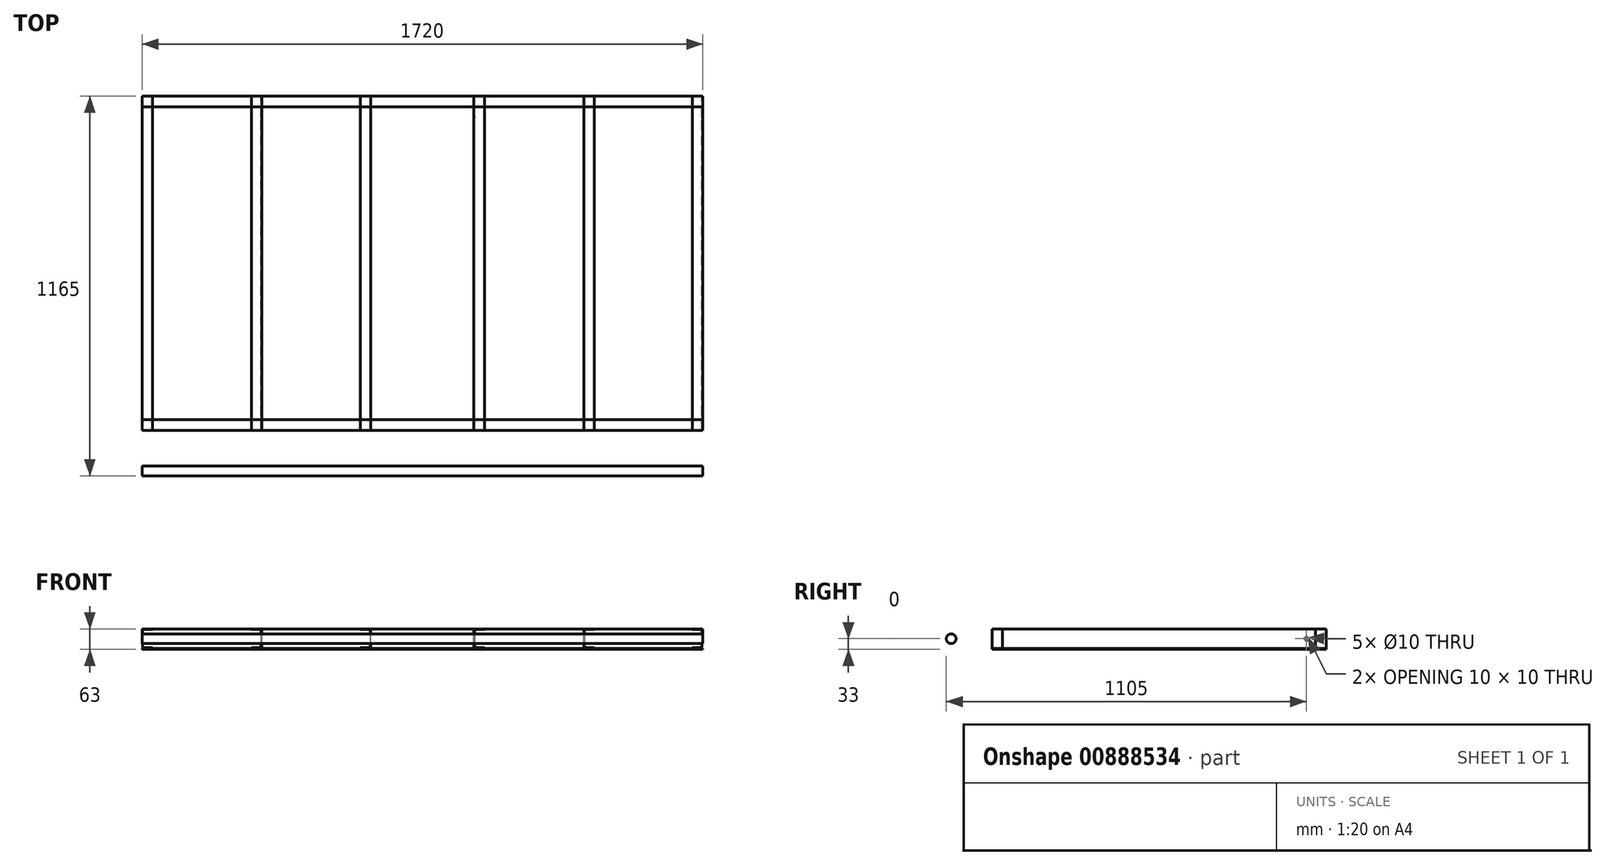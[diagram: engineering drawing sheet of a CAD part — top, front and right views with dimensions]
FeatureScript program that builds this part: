
annotation { "Feature Type Name" : "Feature", "Feature Type Description" : "" }
export const myFeature = defineFeature(function(context is Context, id is Id, definition is map)
    precondition{}
    {
        {
            var Q0;
            Q0=qCreatedBy(makeId("Front.planeOp"),FACE);
            var sketch = newSketch(context, id + "F0", { "sketchPlane" : qUnion([Q0])});
            skLineSegment(sketch, "E0", {"start": v(0, 0) * mm, "end": v(0, 60) * mm});
            skLineSegment(sketch, "E1", {"start": v(0, 60) * mm, "end": v(32, 60) * mm});
            skLineSegment(sketch, "E2.0", {"start": v(2, 58) * mm, "end": v(32, 58) * mm});
            skLineSegment(sketch, "E3", {"start": v(32, 60) * mm, "end": v(32, 58) * mm});
            skLineSegment(sketch, "E4", {"start": v(0, 30) * mm, "end": v(30.45, 30) * mm, "construction": true});
            skLineSegment(sketch, "E5.MirrorCS", {"start": v(32, 0) * mm, "end": v(32, 2) * mm});
            skLineSegment(sketch, "E6.MirrorCS", {"start": v(2, 2) * mm, "end": v(32, 2) * mm});
            skLineSegment(sketch, "E7.MirrorCS", {"start": v(0, 0) * mm, "end": v(32, 0) * mm});
            skLineSegment(sketch, "E8", {"start": v(2, 58) * mm, "end": v(2, 2) * mm});
            skSolve(sketch);
        }
        {
            var Q0;
            Q0=makeQuery(id+"F0.imprint","IMPRINT",FACE,{"disambiguationData":[TD([[makeQuery(id+"F0.imprint","IMPRINT",EDGE,{"derivedFrom":sQuery(id+"F0.wireOp",EDGE,"E0")}),-1.0]])]});
            extrude(context, id + "F1", {"entities" : qUnion([Q0]), "endBound" : BoundingType.SYMMETRIC, "depth" : 1025 * mm, "offsetDistance" : 25 * mm});
        }
        {
            var Q0;
            Q0=makeQuery(id+"F1.opExtrude","SWEPT_BODY",BODY,{"disambiguationData":[OSD([sQuery(id+"F0.wireOp",EDGE,"E0"),sQuery(id+"F0.wireOp",EDGE,"E1"),sQuery(id+"F0.wireOp",EDGE,"E2.0"),sQuery(id+"F0.wireOp",EDGE,"E3"),sQuery(id+"F0.wireOp",EDGE,"E5.MirrorCS"),sQuery(id+"F0.wireOp",EDGE,"E6.MirrorCS"),sQuery(id+"F0.wireOp",EDGE,"E7.MirrorCS"),sQuery(id+"F0.wireOp",EDGE,"E8")])]});
            var Q1;
            Q1=makeQuery(id+"F1.opExtrude","CAP_EDGE",EDGE,{"disambiguationData":[OSD([sQuery(id+"F0.wireOp",EDGE,"E1")])],"isStart":false});
            transform(context, id + "F2", {"entities" : qUnion([Q0]), "transformType" : TransformType.TRANSLATION_DISTANCE, "transformDirection" : qUnion([Q1]), "distance" : 158.25 * mm, "makeCopy" : false});
        }
        {
            var Q0;
            Q0=qCreatedBy(makeId("Top.planeOp"),FACE);
            var sketch = newSketch(context, id + "F3", { "sketchPlane" : qUnion([Q0])});
            skLineSegment(sketch, "E9.bottom", {"start": v(-860, 512.5) * mm, "end": v(860, 512.5) * mm});
            skLineSegment(sketch, "E9.top", {"start": v(-860, -512.5) * mm, "end": v(860, -512.5) * mm});
            skLineSegment(sketch, "E9.left", {"start": v(-860, 512.5) * mm, "end": v(-860, -512.5) * mm});
            skLineSegment(sketch, "E9.right", {"start": v(860, 512.5) * mm, "end": v(860, -512.5) * mm});
            skLineSegment(sketch, "E10", {"start": v(0, -494.46) * mm, "end": v(0, 621.74) * mm, "construction": true});
            skLineSegment(sketch, "E11", {"start": v(-634.69, 0) * mm, "end": v(657.83, 0) * mm, "construction": true});
            skSolve(sketch);
        }
        {
            var Q0;
            Q0 = qSketchRegion(id + "F3", true);
            extrude(context, id + "F4", {"entities" : qUnion([Q0]), "oppositeDirection" : true, "depth" : 3 * mm, "offsetDistance" : 25 * mm});
        }
        {
            var Q0;
            Q0=makeQuery(id+"F1.opExtrude","SWEPT_BODY",BODY,{"disambiguationData":[OSD([sQuery(id+"F0.wireOp",EDGE,"E0"),sQuery(id+"F0.wireOp",EDGE,"E1"),sQuery(id+"F0.wireOp",EDGE,"E2.0"),sQuery(id+"F0.wireOp",EDGE,"E3"),sQuery(id+"F0.wireOp",EDGE,"E5.MirrorCS"),sQuery(id+"F0.wireOp",EDGE,"E6.MirrorCS"),sQuery(id+"F0.wireOp",EDGE,"E7.MirrorCS"),sQuery(id+"F0.wireOp",EDGE,"E8")])]});
            var Q1;
            Q1=makeQuery(id+"F4.opExtrude","CAP_EDGE",EDGE,{"disambiguationData":[OSD([sQuery(id+"F3.wireOp",EDGE,"E9.top")])],"isStart":true});
            transform(context, id + "F5", {"entities" : qUnion([Q0]), "transformType" : TransformType.TRANSLATION_DISTANCE, "transformDirection" : qUnion([Q1]), "distance" : 337 * mm, "makeCopy" : true});
        }
        {
            var Q0;
            Q0=makeQuery(id+"F4.opExtrude","CAP_FACE",FACE,{"disambiguationData":[OSD([sQuery(id+"F3.wireOp",EDGE,"E9.bottom"),sQuery(id+"F3.wireOp",EDGE,"E9.top"),sQuery(id+"F3.wireOp",EDGE,"E9.left"),sQuery(id+"F3.wireOp",EDGE,"E9.right")])],"isStart":true});
            cPlane(context, id + "F6", {"entities" : qUnion([Q0]), "cplaneType" : CPlaneType.OFFSET, "offset" : 0 * mm, "width" : 150 * mm, "height" : 150 * mm});
        }
        {
            var Q0;
            Q0=qCreatedBy(id+"F6.planeOp",FACE);
            var sketch = newSketch(context, id + "F7", { "sketchPlane" : qUnion([Q0])});
            skLineSegment(sketch, "E12.0", {"start": v(527.25, -512.5) * mm, "end": v(527.25, 512.5) * mm, "construction": true});
            skLineSegment(sketch, "E13.0", {"start": v(860, 512.5) * mm, "end": v(860, -512.5) * mm, "construction": true});
            skLineSegment(sketch, "E14", {"start": v(527.25, 0) * mm, "end": v(828, 0) * mm, "construction": true});
            skPoint(sketch, "E15.startSnap0", {"position": v(693.62, 0) * mm});
            skLineSegment(sketch, "E16", {"start": v(828, 189.17) * mm, "end": v(828, -311.1) * mm, "construction": true});
            skPoint(sketch, "E17.orphan", {"position": v(860, 0) * mm});
            skLineSegment(sketch, "E18", {"start": v(677.62, 0) * mm, "end": v(677.62, 369.47) * mm, "construction": true});
            skSolve(sketch);
        }
        {
            var Q0;
            Q0=sQuery(id+"F7.wireOp",EDGE,"E14");
            cPoint(context, id + "F8", {"entities" : qUnion([Q0]), "parameter" : 0.5});
        }
        {
            var Q0;
            Q0 = qCreatedBy(id + "F8" ,VERTEX);
            var Q1;
            Q1=sQuery(id+"F7.wireOp",EDGE,"E14");
            cPlane(context, id + "F9", {"entities" : qUnion([Q0, Q1]), "cplaneType" : CPlaneType.LINE_POINT, "offset" : 25 * mm, "width" : 150 * mm, "height" : 150 * mm});
        }
        {
            var Q0;
            Q0=makeQuery(id+"F5.opPattern","COPY",BODY,{"derivedFrom":makeQuery(id+"F1.opExtrude","SWEPT_BODY",BODY,{"disambiguationData":[OSD([sQuery(id+"F0.wireOp",EDGE,"E0"),sQuery(id+"F0.wireOp",EDGE,"E1"),sQuery(id+"F0.wireOp",EDGE,"E2.0"),sQuery(id+"F0.wireOp",EDGE,"E3"),sQuery(id+"F0.wireOp",EDGE,"E5.MirrorCS"),sQuery(id+"F0.wireOp",EDGE,"E6.MirrorCS"),sQuery(id+"F0.wireOp",EDGE,"E7.MirrorCS"),sQuery(id+"F0.wireOp",EDGE,"E8")])]}),"instanceName":"1"});
            var Q1;
            Q1=qCreatedBy(id+"F9.planeOp",FACE);
            mirror(context, id + "F10", {"entities" : qUnion([Q0]), "mirrorPlane" : qUnion([Q1])});
        }
        {
            var Q0;
            Q0=makeQuery(id+"F1.opExtrude","SWEPT_BODY",BODY,{"disambiguationData":[OSD([sQuery(id+"F0.wireOp",EDGE,"E0"),sQuery(id+"F0.wireOp",EDGE,"E1"),sQuery(id+"F0.wireOp",EDGE,"E2.0"),sQuery(id+"F0.wireOp",EDGE,"E3"),sQuery(id+"F0.wireOp",EDGE,"E5.MirrorCS"),sQuery(id+"F0.wireOp",EDGE,"E6.MirrorCS"),sQuery(id+"F0.wireOp",EDGE,"E7.MirrorCS"),sQuery(id+"F0.wireOp",EDGE,"E8")])]});
            var Q1;
            Q1=makeQuery(id+"F10.opPattern","COPY",BODY,{"derivedFrom":makeQuery(id+"F5.opPattern","COPY",BODY,{"derivedFrom":makeQuery(id+"F1.opExtrude","SWEPT_BODY",BODY,{"disambiguationData":[OSD([sQuery(id+"F0.wireOp",EDGE,"E0"),sQuery(id+"F0.wireOp",EDGE,"E1"),sQuery(id+"F0.wireOp",EDGE,"E2.0"),sQuery(id+"F0.wireOp",EDGE,"E3"),sQuery(id+"F0.wireOp",EDGE,"E5.MirrorCS"),sQuery(id+"F0.wireOp",EDGE,"E6.MirrorCS"),sQuery(id+"F0.wireOp",EDGE,"E7.MirrorCS"),sQuery(id+"F0.wireOp",EDGE,"E8")])]}),"instanceName":"1"}),"instanceName":"1"});
            var Q2;
            Q2=qCreatedBy(makeId("Right.planeOp"),FACE);
            mirror(context, id + "F11", {"entities" : qUnion([Q0, Q1]), "mirrorPlane" : qUnion([Q2])});
        }
        {
            var Q0;
            Q0=makeQuery(id+"F5.opPattern","COPY",FACE,{"derivedFrom":makeQuery(id+"F1.opExtrude","SWEPT_FACE",FACE,{"disambiguationData":[OSD([sQuery(id+"F0.wireOp",EDGE,"E0")])]}),"instanceName":"1"});
            var sketch = newSketch(context, id + "F12", { "sketchPlane" : qUnion([Q0])});
            skCircle(sketch, "E19", {"center": v(-452.5, 30) * mm, "radius": 5 * mm});
            skSolve(sketch);
        }
        {
            var Q0;
            Q0 = qSketchRegion(id + "F12", true);
            extrude(context, id + "F13", {"entities" : qUnion([Q0]), "operationType" : NewBodyOperationType.REMOVE, "endBound" : BoundingType.SYMMETRIC, "oppositeDirection" : true, "depth" : 2000 * mm, "offsetDistance" : 25 * mm});
        }
        {
            var Q0;
            Q0=makeQuery(id+"F11.opPattern","COPY",BODY,{"derivedFrom":makeQuery(id+"F1.opExtrude","SWEPT_BODY",BODY,{"disambiguationData":[OSD([sQuery(id+"F0.wireOp",EDGE,"E0"),sQuery(id+"F0.wireOp",EDGE,"E1"),sQuery(id+"F0.wireOp",EDGE,"E2.0"),sQuery(id+"F0.wireOp",EDGE,"E3"),sQuery(id+"F0.wireOp",EDGE,"E5.MirrorCS"),sQuery(id+"F0.wireOp",EDGE,"E6.MirrorCS"),sQuery(id+"F0.wireOp",EDGE,"E7.MirrorCS"),sQuery(id+"F0.wireOp",EDGE,"E8")])]}),"instanceName":"1"});
            transform(context, id + "F14", {"entities" : qUnion([Q0]), "transformType" : TransformType.TRANSLATION_3D, "dx" : -334.5 * mm, "dy" : 0 * mm, "dz" : 0 * mm, "makeCopy" : true});
        }
        {
            var Q0;
            Q0=makeQuery(id+"F10.opPattern","COPY",FACE,{"derivedFrom":makeQuery(id+"F5.opPattern","COPY",FACE,{"derivedFrom":makeQuery(id+"F1.opExtrude","SWEPT_FACE",FACE,{"disambiguationData":[OSD([sQuery(id+"F0.wireOp",EDGE,"E0")])]}),"instanceName":"1"}),"instanceName":"1"});
            var sketch = newSketch(context, id + "F15", { "sketchPlane" : qUnion([Q0])});
            skCircle(sketch, "E20", {"center": v(-637.5, 30) * mm, "radius": 15 * mm});
            skSolve(sketch);
        }
        {
            var Q0;
            Q0 = qSketchRegion(id + "F15", true);
            var Q1;
            Q1=makeQuery(id+"F11.opPattern","COPY",FACE,{"derivedFrom":makeQuery(id+"F10.opPattern","COPY",FACE,{"derivedFrom":makeQuery(id+"F5.opPattern","COPY",FACE,{"derivedFrom":makeQuery(id+"F1.opExtrude","SWEPT_FACE",FACE,{"disambiguationData":[OSD([sQuery(id+"F0.wireOp",EDGE,"E0")])]}),"instanceName":"1"}),"instanceName":"1"}),"instanceName":"1"});
            extrude(context, id + "F16", {"entities" : qUnion([Q0]), "endBound" : BoundingType.UP_TO_SURFACE, "oppositeDirection" : true, "depth" : 25 * mm, "endBoundEntityFace" : qUnion([Q1]), "offsetDistance" : 25 * mm});
        }
        {
            var Q0;
            Q0=makeQuery(id+"F10.opPattern","COPY",FACE,{"derivedFrom":makeQuery(id+"F5.opPattern","COPY",FACE,{"derivedFrom":makeQuery(id+"F1.opExtrude","SWEPT_FACE",FACE,{"disambiguationData":[OSD([sQuery(id+"F0.wireOp",EDGE,"E0")])]}),"instanceName":"1"}),"instanceName":"1"});
            var sketch = newSketch(context, id + "F17", { "sketchPlane" : qUnion([Q0])});
            skLineSegment(sketch, "E21.bottom", {"start": v(512.5, 60) * mm, "end": v(480.5, 60) * mm});
            skLineSegment(sketch, "E21.top", {"start": v(512.5, 0) * mm, "end": v(480.5, 0) * mm});
            skLineSegment(sketch, "E21.left", {"start": v(512.5, 60) * mm, "end": v(512.5, 0) * mm});
            skLineSegment(sketch, "E21.right", {"start": v(480.5, 60) * mm, "end": v(480.5, 0) * mm});
            skSolve(sketch);
        }
        {
            var Q0;
            Q0 = qSketchRegion(id + "F17", true);
            var Q1;
            Q1=makeQuery(id+"F11.opPattern","COPY",FACE,{"derivedFrom":makeQuery(id+"F10.opPattern","COPY",FACE,{"derivedFrom":makeQuery(id+"F5.opPattern","COPY",FACE,{"derivedFrom":makeQuery(id+"F1.opExtrude","SWEPT_FACE",FACE,{"disambiguationData":[OSD([sQuery(id+"F0.wireOp",EDGE,"E0")])]}),"instanceName":"1"}),"instanceName":"1"}),"instanceName":"1"});
            extrude(context, id + "F18", {"entities" : qUnion([Q0]), "endBound" : BoundingType.UP_TO_SURFACE, "oppositeDirection" : true, "depth" : 25 * mm, "endBoundEntityFace" : qUnion([Q1]), "offsetDistance" : 25 * mm});
        }
        {
            var Q0;
            Q0=makeQuery(id+"F18.opExtrude","SWEPT_BODY",BODY,{"disambiguationData":[OSD([sQuery(id+"F17.wireOp",EDGE,"E21.bottom"),sQuery(id+"F17.wireOp",EDGE,"E21.top"),sQuery(id+"F17.wireOp",EDGE,"E21.left"),sQuery(id+"F17.wireOp",EDGE,"E21.right")])]});
            var Q1;
            Q1=qCreatedBy(makeId("Front.planeOp"),FACE);
            mirror(context, id + "F19", {"entities" : qUnion([Q0]), "mirrorPlane" : qUnion([Q1])});
        }
    });
